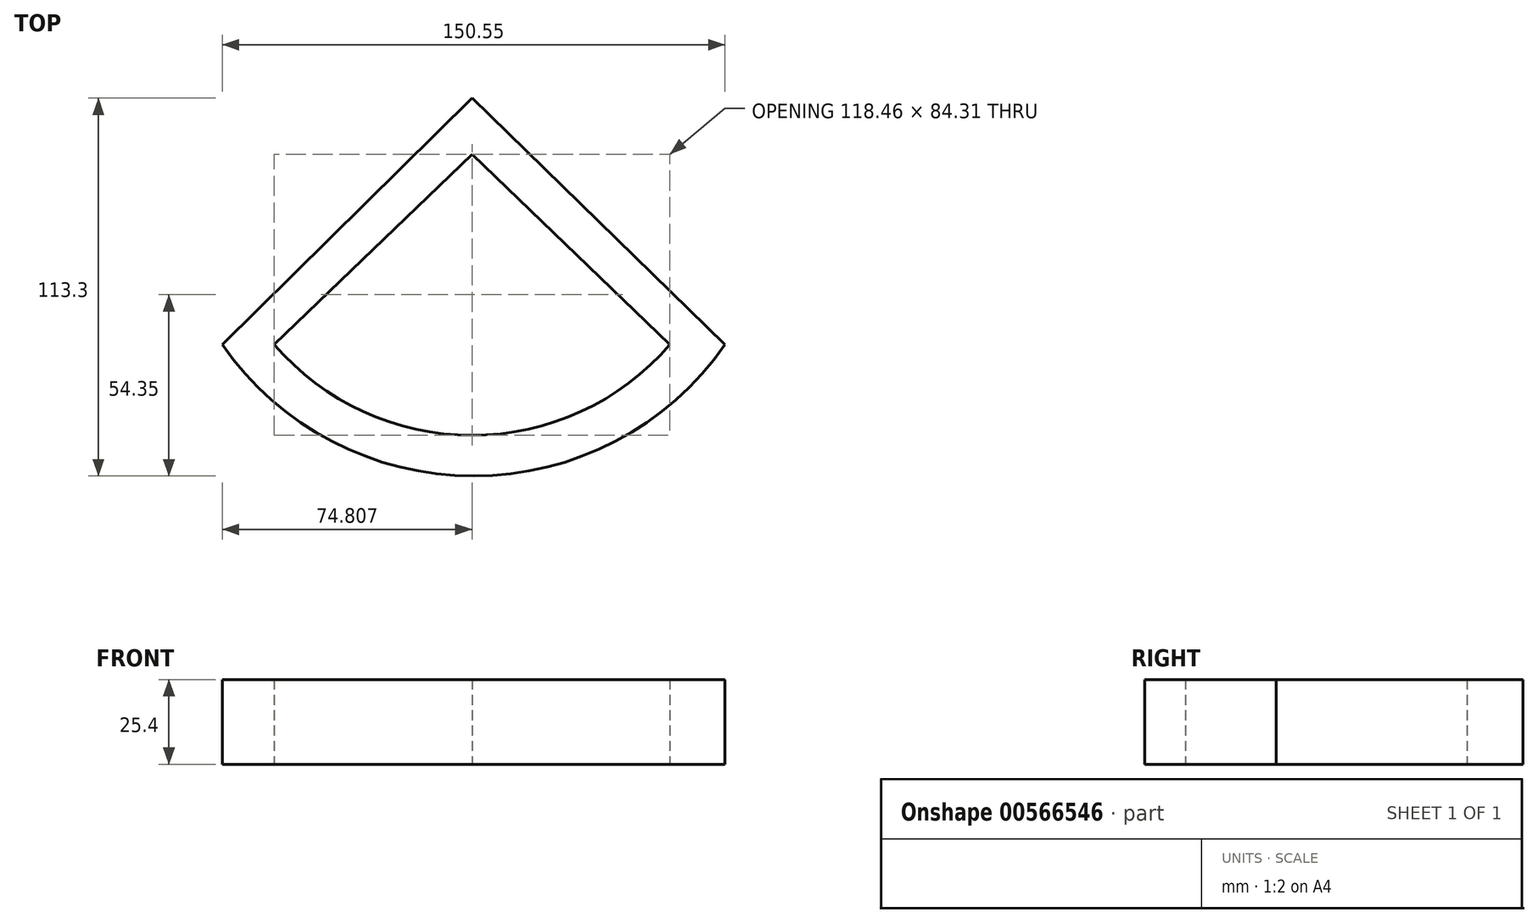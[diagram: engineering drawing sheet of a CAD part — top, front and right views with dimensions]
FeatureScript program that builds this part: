
annotation { "Feature Type Name" : "Feature", "Feature Type Description" : "" }
export const myFeature = defineFeature(function(context is Context, id is Id, definition is map)
    precondition{}
    {
        {
            var Q0;
            Q0=qCreatedBy(makeId("Top.planeOp"),FACE);
            var sketch = newSketch(context, id + "F0", { "sketchPlane" : qUnion([Q0])});
            skLineSegment(sketch, "E0", {"start": v(0, 73.9) * mm, "end": v(-74.82, 0) * mm});
            skLineSegment(sketch, "E1", {"start": v(0, 73.9) * mm, "end": v(75.73, 0) * mm});
            skArc(sketch, "E2", {"start": v(-74.82, 0) * mm, "mid": v(0.46, -39.4) * mm, "end": v(75.73, 0) * mm});
            skSolve(sketch);
        }
        {
            var Q0;
            Q0 = qSketchRegion(id + "F0", true);
            extrude(context, id + "F1", {"entities" : qUnion([Q0]), "depth" : 25.4 * mm, "offsetDistance" : 25.4 * mm});
        }
        {
            var Q0;
            Q0=qCreatedBy(makeId("Top.planeOp"),FACE);
            var sketch = newSketch(context, id + "F2", { "sketchPlane" : qUnion([Q0])});
            skLineSegment(sketch, "E3", {"start": v(0, 62.9) * mm, "end": v(-62.3, 0) * mm});
            skLineSegment(sketch, "E4", {"start": v(-62.3, -0.3) * mm, "end": v(0, 62.9) * mm});
            skLineSegment(sketch, "E5", {"start": v(0, 62.9) * mm, "end": v(63.83, 0) * mm});
            skArc(sketch, "E6", {"start": v(-62.3, 0) * mm, "mid": v(0.77, -31.89) * mm, "end": v(63.83, 0) * mm});
            skSolve(sketch);
        }
        {
            var Q0;
            {var subQ0=sQuery(id+"F2.wireOp",EDGE,"E5");Q0=makeQuery(id+"F2.imprint","IMPRINT",FACE,{"disambiguationData":[TD([[makeQuery(id+"F2.imprint","IMPRINT",EDGE,{"derivedFrom":subQ0}),-1.0]])]});}
            extrude(context, id + "F3", {"entities" : qUnion([Q0]), "operationType" : NewBodyOperationType.REMOVE, "oppositeDirection" : true, "depth" : 25.4 * mm, "offsetDistance" : 25.4 * mm});
        }
        {
            var Q0;
            Q0=qCreatedBy(makeId("Top.planeOp"),FACE);
            var sketch = newSketch(context, id + "F4", { "sketchPlane" : qUnion([Q0])});
            skLineSegment(sketch, "E7", {"start": v(0, 57.1) * mm, "end": v(-59.24, 0) * mm});
            skLineSegment(sketch, "E8", {"start": v(0, 57.1) * mm, "end": v(59.22, 0) * mm});
            skArc(sketch, "E9", {"start": v(-59.24, 0) * mm, "mid": v(-0.01, -27.2) * mm, "end": v(59.22, 0) * mm});
            skSolve(sketch);
        }
        {
            var Q0;
            Q0 = qSketchRegion(id + "F4", true);
            extrude(context, id + "F5", {"entities" : qUnion([Q0]), "operationType" : NewBodyOperationType.REMOVE, "depth" : 25.4 * mm, "offsetDistance" : 25.4 * mm});
        }
    });
